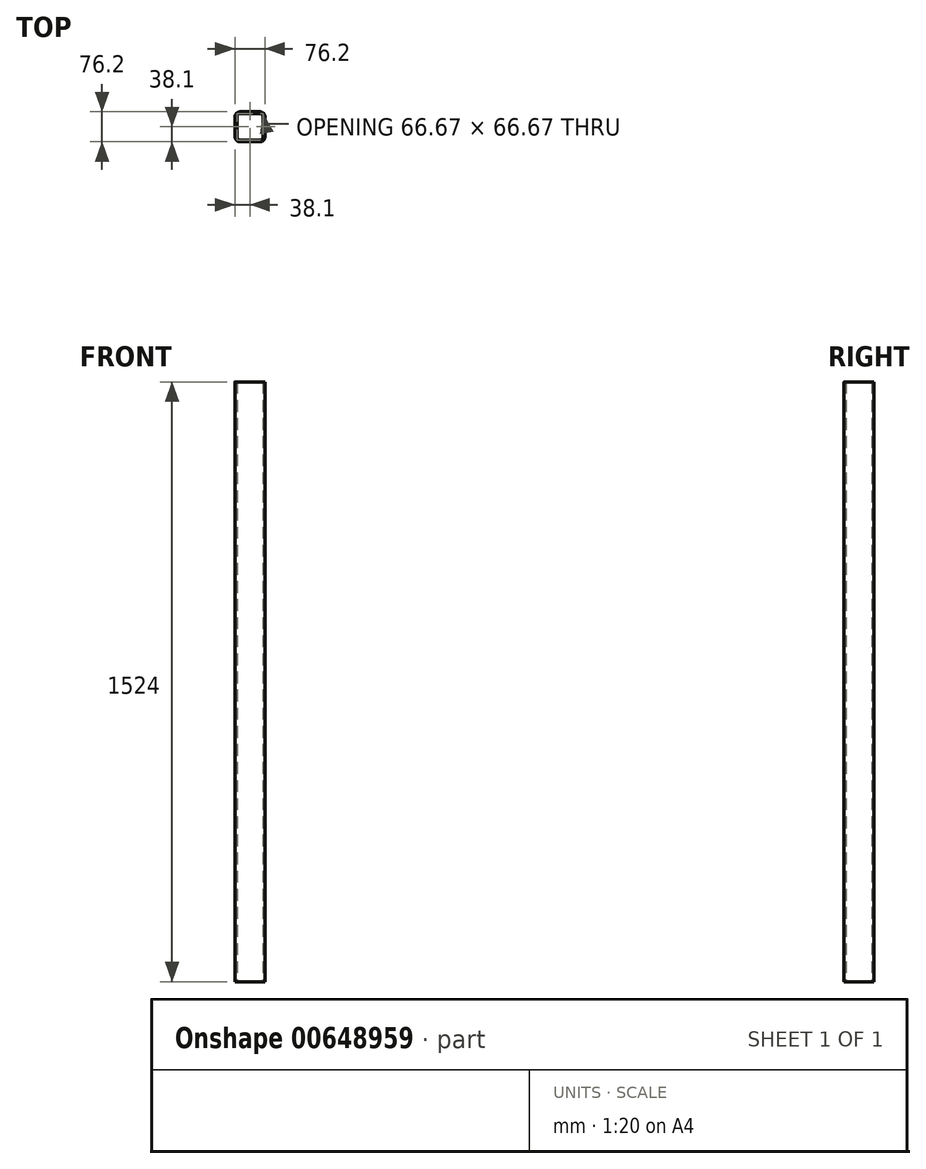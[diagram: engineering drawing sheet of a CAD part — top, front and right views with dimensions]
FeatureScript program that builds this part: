
annotation { "Feature Type Name" : "Feature", "Feature Type Description" : "" }
export const myFeature = defineFeature(function(context is Context, id is Id, definition is map)
    precondition{}
    {
        {
            var Q0;
            Q0=qCreatedBy(makeId("Top.planeOp"),FACE);
            var sketch = newSketch(context, id + "F0", { "sketchPlane" : qUnion([Q0])});
            skLineSegment(sketch, "E0.bottom", {"start": v(25.4, 38.1) * mm, "end": v(-25.4, 38.1) * mm});
            skLineSegment(sketch, "E0.top", {"start": v(25.4, -38.1) * mm, "end": v(-25.4, -38.1) * mm});
            skLineSegment(sketch, "E0.left", {"start": v(38.1, 25.4) * mm, "end": v(38.1, -25.4) * mm});
            skLineSegment(sketch, "E0.right", {"start": v(-38.1, 25.4) * mm, "end": v(-38.1, -25.4) * mm});
            skPoint(sketch, "E0.middle", {"position": v(0, 0) * mm});
            skPoint(sketch, "E1.visualSharp", {"position": v(38.1, 38.1) * mm});
            skArc(sketch, "E1.filletArc", {"start": v(38.1, 25.4) * mm, "mid": v(34.38, 34.38) * mm, "end": v(25.4, 38.1) * mm});
            skPoint(sketch, "E2.visualSharp", {"position": v(-38.1, 38.1) * mm});
            skArc(sketch, "E2.filletArc", {"start": v(-25.4, 38.1) * mm, "mid": v(-34.38, 34.38) * mm, "end": v(-38.1, 25.4) * mm});
            skPoint(sketch, "E3.visualSharp", {"position": v(-38.1, -38.1) * mm});
            skArc(sketch, "E3.filletArc", {"start": v(-38.1, -25.4) * mm, "mid": v(-34.38, -34.38) * mm, "end": v(-25.4, -38.1) * mm});
            skPoint(sketch, "E4.visualSharp", {"position": v(38.1, -38.1) * mm});
            skArc(sketch, "E4.filletArc", {"start": v(25.4, -38.1) * mm, "mid": v(34.38, -34.38) * mm, "end": v(38.1, -25.4) * mm});
            skArc(sketch, "E5.0", {"start": v(33.34, 25.4) * mm, "mid": v(31.01, 31.01) * mm, "end": v(25.4, 33.34) * mm});
            skLineSegment(sketch, "E5.1", {"start": v(33.34, 25.4) * mm, "end": v(33.34, -25.4) * mm});
            skLineSegment(sketch, "E5.2", {"start": v(25.4, 33.34) * mm, "end": v(-25.4, 33.34) * mm});
            skArc(sketch, "E5.3", {"start": v(25.4, -33.34) * mm, "mid": v(31.01, -31.01) * mm, "end": v(33.34, -25.4) * mm});
            skArc(sketch, "E5.4", {"start": v(-25.4, 33.34) * mm, "mid": v(-31.01, 31.01) * mm, "end": v(-33.34, 25.4) * mm});
            skLineSegment(sketch, "E5.5", {"start": v(-33.34, 25.4) * mm, "end": v(-33.34, -25.4) * mm});
            skArc(sketch, "E5.6", {"start": v(-33.34, -25.4) * mm, "mid": v(-31.01, -31.01) * mm, "end": v(-25.4, -33.34) * mm});
            skLineSegment(sketch, "E5.7", {"start": v(25.4, -33.34) * mm, "end": v(-25.4, -33.34) * mm});
            skSolve(sketch);
        }
        {
            var Q0;
            Q0 = qSketchRegion(id + "F0", true);
            extrude(context, id + "F1", {"entities" : qUnion([Q0]), "depth" : 1524 * mm, "offsetDistance" : 25.4 * mm});
        }
    });
